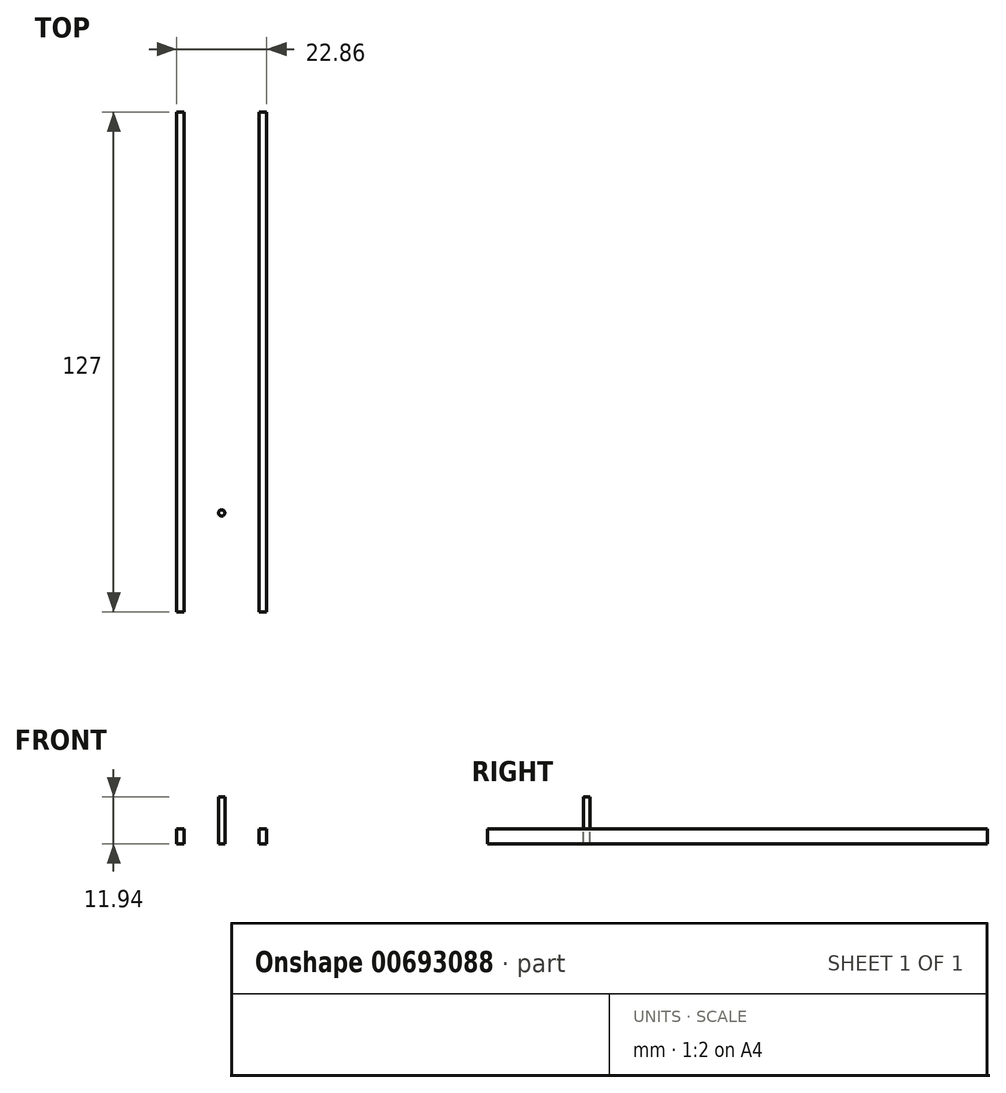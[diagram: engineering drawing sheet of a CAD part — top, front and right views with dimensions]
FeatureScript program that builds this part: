
annotation { "Feature Type Name" : "Feature", "Feature Type Description" : "" }
export const myFeature = defineFeature(function(context is Context, id is Id, definition is map)
    precondition{}
    {
        {
            var Q0;
            Q0=qCreatedBy(makeId("Front.planeOp"),FACE);
            var sketch = newSketch(context, id + "F0", { "sketchPlane" : qUnion([Q0])});
            skLineSegment(sketch, "E0", {"start": v(0, 0) * mm, "end": v(-11.43, 0) * mm});
            skLineSegment(sketch, "E1", {"start": v(0, 0) * mm, "end": v(11.43, 0) * mm});
            skLineSegment(sketch, "E2", {"start": v(11.43, 0) * mm, "end": v(11.43, 3.83) * mm});
            skLineSegment(sketch, "E3", {"start": v(11.43, 3.83) * mm, "end": v(9.53, 3.83) * mm});
            skLineSegment(sketch, "E4", {"start": v(9.53, 3.83) * mm, "end": v(9.53, 11.94) * mm});
            skLineSegment(sketch, "E5", {"start": v(9.53, 11.94) * mm, "end": v(-9.53, 11.94) * mm});
            skLineSegment(sketch, "E6", {"start": v(-9.53, 11.94) * mm, "end": v(-9.53, 3.83) * mm});
            skLineSegment(sketch, "E7", {"start": v(-11.43, 0) * mm, "end": v(-11.43, 3.83) * mm});
            skLineSegment(sketch, "E8", {"start": v(-11.43, 3.83) * mm, "end": v(-9.53, 3.83) * mm});
            skSolve(sketch);
        }
        {
            var Q0;
            Q0=makeQuery(id+"F0.imprint","IMPRINT",FACE,{"disambiguationData":[TD([[makeQuery(id+"F0.imprint","IMPRINT",EDGE,{"derivedFrom":sQuery(id+"F0.wireOp",EDGE,"E0")}),-1.0]])]});
            extrude(context, id + "F1", {"entities" : qUnion([Q0]), "depth" : 127 * mm, "offsetDistance" : 25.4 * mm});
        }
        {
            var Q0;
            Q0=makeQuery(id+"F1.opExtrude","SWEPT_FACE",FACE,{"disambiguationData":[OSD([sQuery(id+"F0.wireOp",EDGE,"E5")])]});
            var sketch = newSketch(context, id + "F2", { "sketchPlane" : qUnion([Q0])});
            skLineSegment(sketch, "E9", {"start": v(0, 0) * mm, "end": v(0, -127) * mm});
            skCircle(sketch, "E10", {"center": v(0, -116.06) * mm, "radius": 0.8 * mm});
            skCircle(sketch, "E11", {"center": v(0, -101.84) * mm, "radius": 0.8 * mm});
            skSolve(sketch);
        }
        {
            var Q0;
            {var subQ0=sQuery(id+"F2.wireOp",EDGE,"E11");var subQ1=sQuery(id+"F2.wireOp",EDGE,"E9");var subQ2=makeQuery(id+"F2.imprint","INTERSECT",VERTEX,{"disambiguationData":[OD(0.0)],"derivedFrom":[subQ1,subQ0]});Q0=makeQuery(id+"F2.imprint","IMPRINT",FACE,{"disambiguationData":[TD([[makeQuery(id+"F2.imprint","IMPRINT",EDGE,{"disambiguationData":[TD([[subQ2,-1.0]])],"derivedFrom":subQ1}),1.0]])]});}
            var Q1;
            {var subQ0=sQuery(id+"F2.wireOp",EDGE,"E11");var subQ1=sQuery(id+"F2.wireOp",EDGE,"E9");var subQ2=makeQuery(id+"F2.imprint","INTERSECT",VERTEX,{"disambiguationData":[OD(0.0)],"derivedFrom":[subQ1,subQ0]});Q1=makeQuery(id+"F2.imprint","IMPRINT",FACE,{"disambiguationData":[TD([[makeQuery(id+"F2.imprint","IMPRINT",EDGE,{"disambiguationData":[TD([[subQ2,-1.0]])],"derivedFrom":subQ1}),-1.0]])]});}
            var Q2;
            {var subQ0=sQuery(id+"F2.wireOp",EDGE,"E10");var subQ1=sQuery(id+"F2.wireOp",EDGE,"E9");var subQ2=makeQuery(id+"F2.imprint","INTERSECT",VERTEX,{"disambiguationData":[OD(0.0)],"derivedFrom":[subQ1,subQ0]});Q2=makeQuery(id+"F2.imprint","IMPRINT",FACE,{"disambiguationData":[TD([[makeQuery(id+"F2.imprint","IMPRINT",EDGE,{"disambiguationData":[TD([[subQ2,-1.0]])],"derivedFrom":subQ1}),-1.0]])]});}
            var Q3;
            {var subQ0=sQuery(id+"F2.wireOp",EDGE,"E10");var subQ1=sQuery(id+"F2.wireOp",EDGE,"E9");var subQ2=makeQuery(id+"F2.imprint","INTERSECT",VERTEX,{"disambiguationData":[OD(0.0)],"derivedFrom":[subQ1,subQ0]});Q3=makeQuery(id+"F2.imprint","IMPRINT",FACE,{"disambiguationData":[TD([[makeQuery(id+"F2.imprint","IMPRINT",EDGE,{"disambiguationData":[TD([[subQ2,-1.0]])],"derivedFrom":subQ1}),1.0]])]});}
            extrude(context, id + "F3", {"entities" : qUnion([Q0, Q1, Q2, Q3]), "operationType" : NewBodyOperationType.REMOVE, "oppositeDirection" : true, "depth" : 25.4 * mm, "offsetDistance" : 25.4 * mm});
        }
    });
